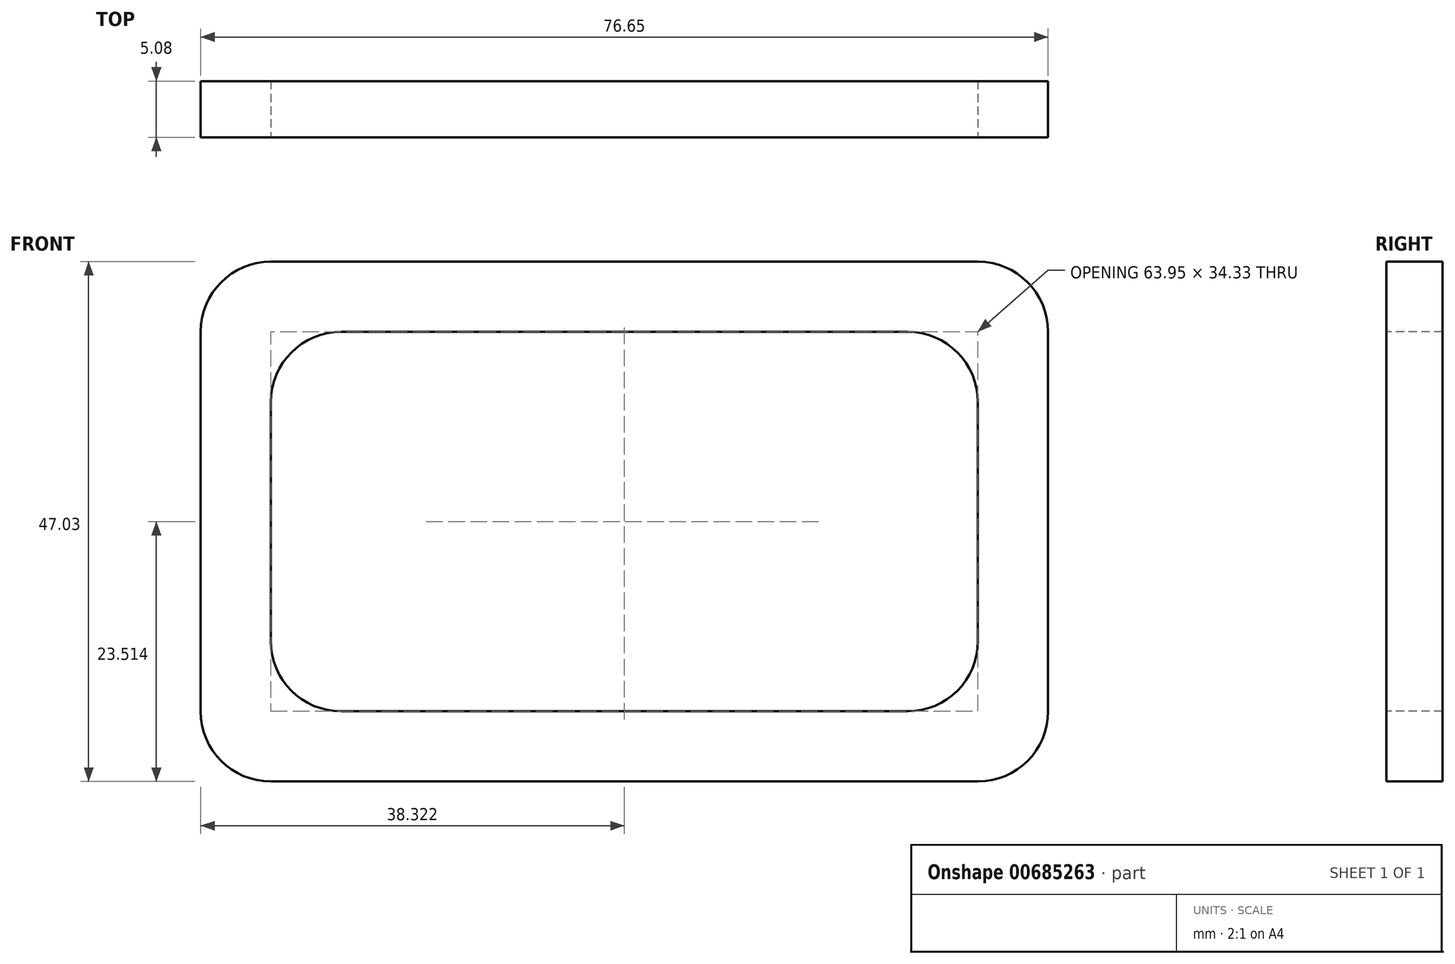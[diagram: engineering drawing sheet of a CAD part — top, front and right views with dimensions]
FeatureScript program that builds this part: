
annotation { "Feature Type Name" : "Feature", "Feature Type Description" : "" }
export const myFeature = defineFeature(function(context is Context, id is Id, definition is map)
    precondition{}
    {
        {
            var Q0;
            Q0=qCreatedBy(makeId("Front.planeOp"),FACE);
            var sketch = newSketch(context, id + "F0", { "sketchPlane" : qUnion([Q0])});
            skLineSegment(sketch, "E0.bottom", {"start": v(-46.02, 12.98) * mm, "end": v(17.93, 12.98) * mm});
            skLineSegment(sketch, "E0.top", {"start": v(-46.02, -34.05) * mm, "end": v(17.93, -34.05) * mm});
            skLineSegment(sketch, "E0.left", {"start": v(-52.37, 6.63) * mm, "end": v(-52.37, -27.7) * mm});
            skLineSegment(sketch, "E0.right", {"start": v(24.28, 6.63) * mm, "end": v(24.28, -27.7) * mm});
            skPoint(sketch, "E1.visualSharp", {"position": v(-52.37, 12.98) * mm});
            skArc(sketch, "E1.filletArc", {"start": v(-46.02, 12.98) * mm, "mid": v(-50.51, 11.12) * mm, "end": v(-52.37, 6.63) * mm});
            skPoint(sketch, "E2.visualSharp", {"position": v(24.28, 12.98) * mm});
            skArc(sketch, "E2.filletArc", {"start": v(24.28, 6.63) * mm, "mid": v(22.42, 11.12) * mm, "end": v(17.93, 12.98) * mm});
            skPoint(sketch, "E3.visualSharp", {"position": v(24.28, -34.05) * mm});
            skArc(sketch, "E3.filletArc", {"start": v(17.93, -34.05) * mm, "mid": v(22.42, -32.2) * mm, "end": v(24.28, -27.7) * mm});
            skPoint(sketch, "E4.visualSharp", {"position": v(-52.37, -34.05) * mm});
            skArc(sketch, "E4.filletArc", {"start": v(-52.37, -27.7) * mm, "mid": v(-50.51, -32.2) * mm, "end": v(-46.02, -34.05) * mm});
            skLineSegment(sketch, "E5.bottom", {"start": v(-39.67, 6.63) * mm, "end": v(11.58, 6.63) * mm});
            skLineSegment(sketch, "E5.top", {"start": v(-39.67, -27.7) * mm, "end": v(11.58, -27.7) * mm});
            skLineSegment(sketch, "E5.left", {"start": v(-46.02, 0.28) * mm, "end": v(-46.02, -21.35) * mm});
            skLineSegment(sketch, "E5.right", {"start": v(17.93, 0.28) * mm, "end": v(17.93, -21.35) * mm});
            skArc(sketch, "E6.filletArc", {"start": v(-39.67, 6.63) * mm, "mid": v(-44.16, 4.77) * mm, "end": v(-46.02, 0.28) * mm});
            skArc(sketch, "E7.filletArc", {"start": v(-46.02, -21.35) * mm, "mid": v(-44.16, -25.84) * mm, "end": v(-39.67, -27.7) * mm});
            skArc(sketch, "E8.filletArc", {"start": v(11.58, -27.7) * mm, "mid": v(16.07, -25.84) * mm, "end": v(17.93, -21.35) * mm});
            skArc(sketch, "E9.filletArc", {"start": v(17.93, 0.28) * mm, "mid": v(16.07, 4.77) * mm, "end": v(11.58, 6.63) * mm});
            skSolve(sketch);
        }
        {
            var Q0;
            Q0=makeQuery(id+"F0.imprint","IMPRINT",FACE,{"disambiguationData":[TD([[makeQuery(id+"F0.imprint","IMPRINT",EDGE,{"derivedFrom":sQuery(id+"F0.wireOp",EDGE,"E0.bottom")}),-1.0]])]});
            extrude(context, id + "F1", {"entities" : qUnion([Q0]), "oppositeDirection" : true, "depth" : 5.08 * mm, "offsetDistance" : 25.4 * mm});
        }
    });
